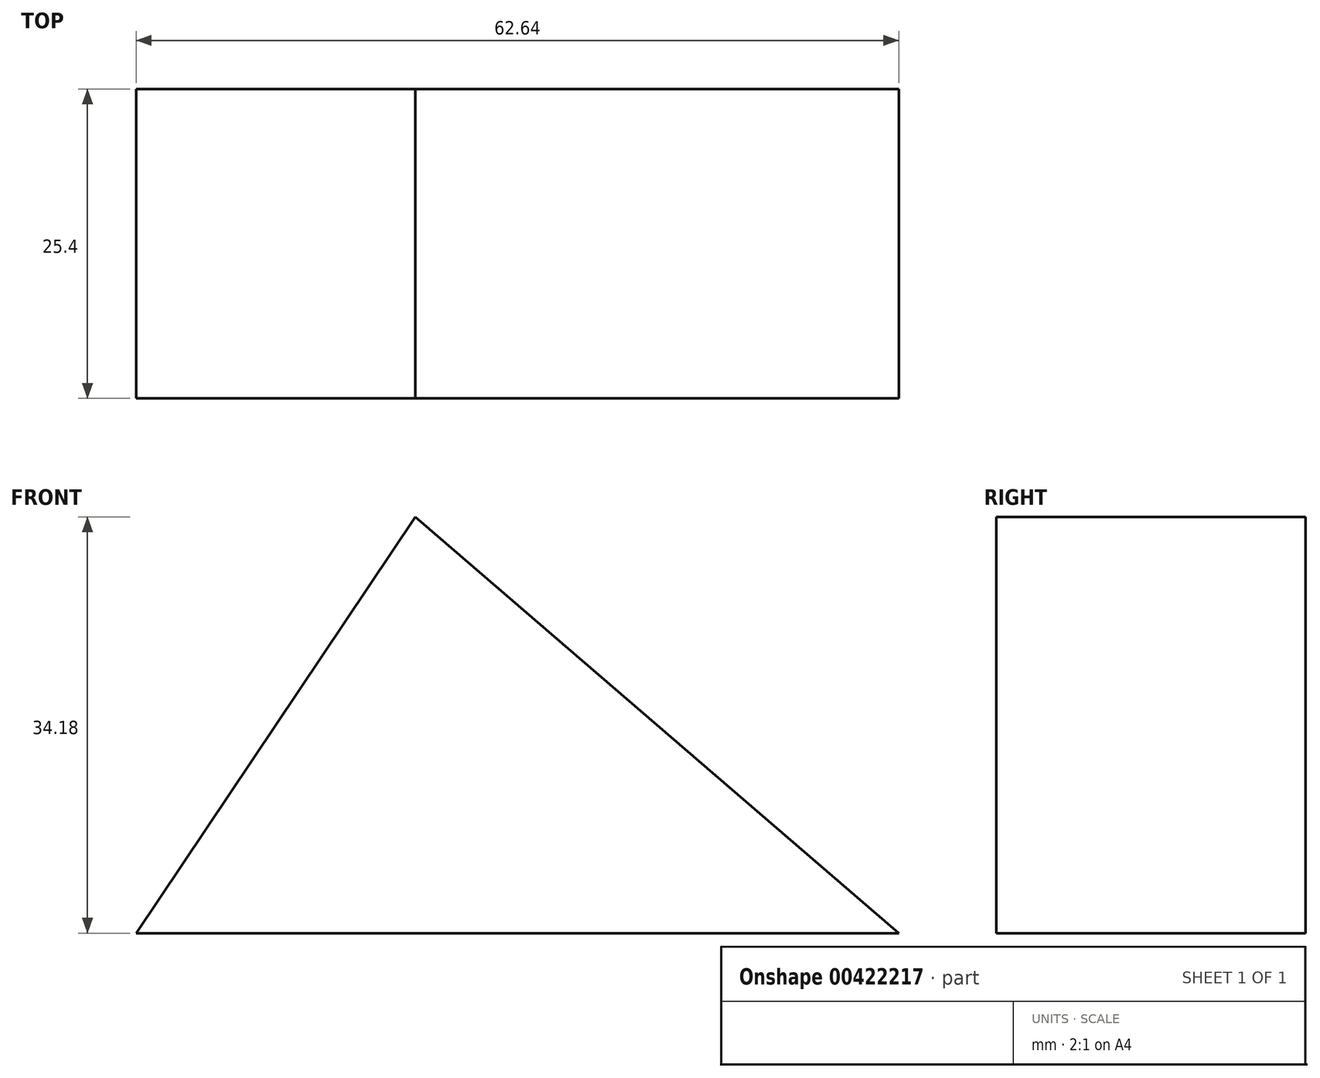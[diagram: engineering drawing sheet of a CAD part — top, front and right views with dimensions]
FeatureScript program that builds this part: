
annotation { "Feature Type Name" : "Feature", "Feature Type Description" : "" }
export const myFeature = defineFeature(function(context is Context, id is Id, definition is map)
    precondition{}
    {
        {
            var Q0;
            Q0=qCreatedBy(makeId("Front.planeOp"),FACE);
            var sketch = newSketch(context, id + "F0", { "sketchPlane" : qUnion([Q0])});
            skLineSegment(sketch, "E0", {"start": v(0, 0) * mm, "end": v(-62.64, 0) * mm});
            skLineSegment(sketch, "E1", {"start": v(-62.64, 0) * mm, "end": v(-39.72, 34.18) * mm});
            skLineSegment(sketch, "E2", {"start": v(-39.72, 34.18) * mm, "end": v(0, 0) * mm});
            skSolve(sketch);
        }
        {
            var Q0;
            Q0 = qSketchRegion(id + "F0", true);
            extrude(context, id + "F1", {"entities" : qUnion([Q0]), "depth" : 25.4 * mm});
        }
    });
